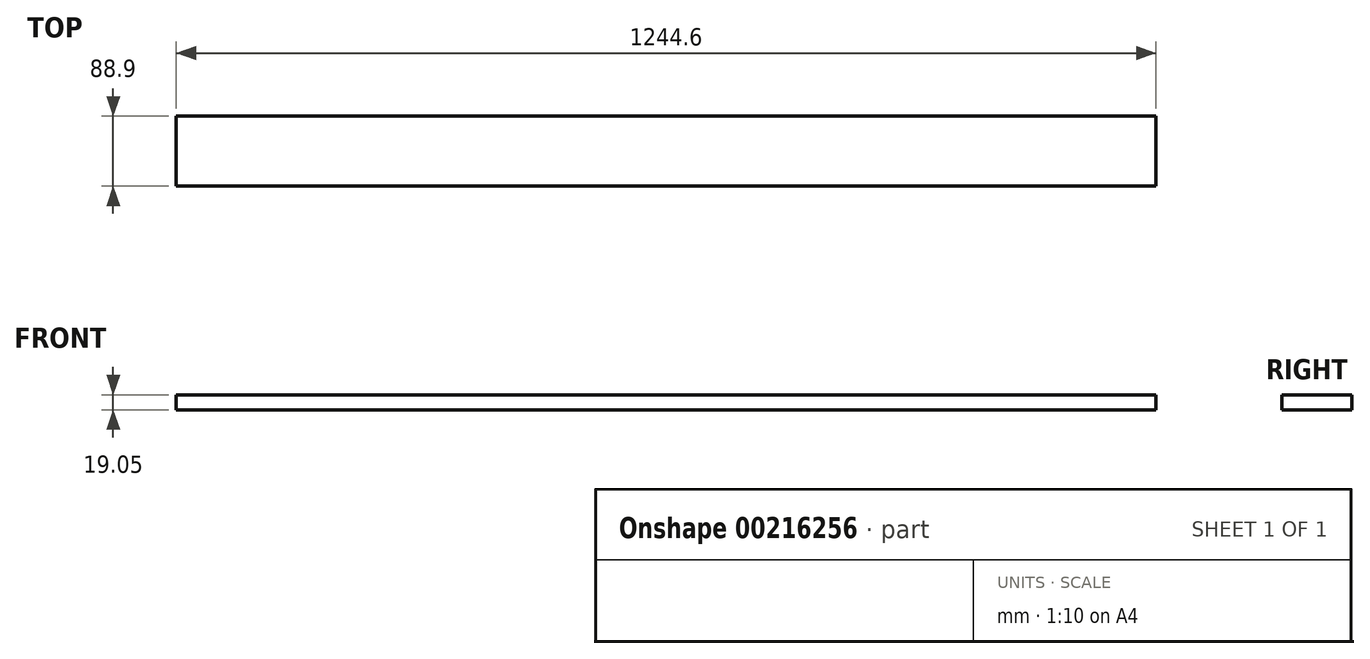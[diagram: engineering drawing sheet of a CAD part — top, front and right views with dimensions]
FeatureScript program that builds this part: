
annotation { "Feature Type Name" : "Feature", "Feature Type Description" : "" }
export const myFeature = defineFeature(function(context is Context, id is Id, definition is map)
    precondition{}
    {
        {
            var Q0;
            Q0=qCreatedBy(makeId("Top.planeOp"),FACE);
            var sketch = newSketch(context, id + "F0", { "sketchPlane" : qUnion([Q0])});
            skLineSegment(sketch, "E0", {"start": v(-4322.73, -2746.5) * mm, "end": v(-3078.13, -2746.5) * mm});
            skLineSegment(sketch, "E1", {"start": v(-3078.13, -2746.5) * mm, "end": v(-3078.13, -2835.4) * mm});
            skLineSegment(sketch, "E2", {"start": v(-3078.13, -2835.4) * mm, "end": v(-4322.73, -2835.4) * mm});
            skLineSegment(sketch, "E3", {"start": v(-4322.73, -2835.4) * mm, "end": v(-4322.73, -2746.5) * mm});
            skSolve(sketch);
        }
        {
            var Q0;
            Q0=makeQuery(id+"F0.imprint","IMPRINT",FACE,{"disambiguationData":[TD([[makeQuery(id+"F0.imprint","IMPRINT",EDGE,{"derivedFrom":sQuery(id+"F0.wireOp",EDGE,"E0")}),-1.0]])]});
            extrude(context, id + "F1", {"entities" : qUnion([Q0]), "depth" : 19.05 * mm});
        }
    });
